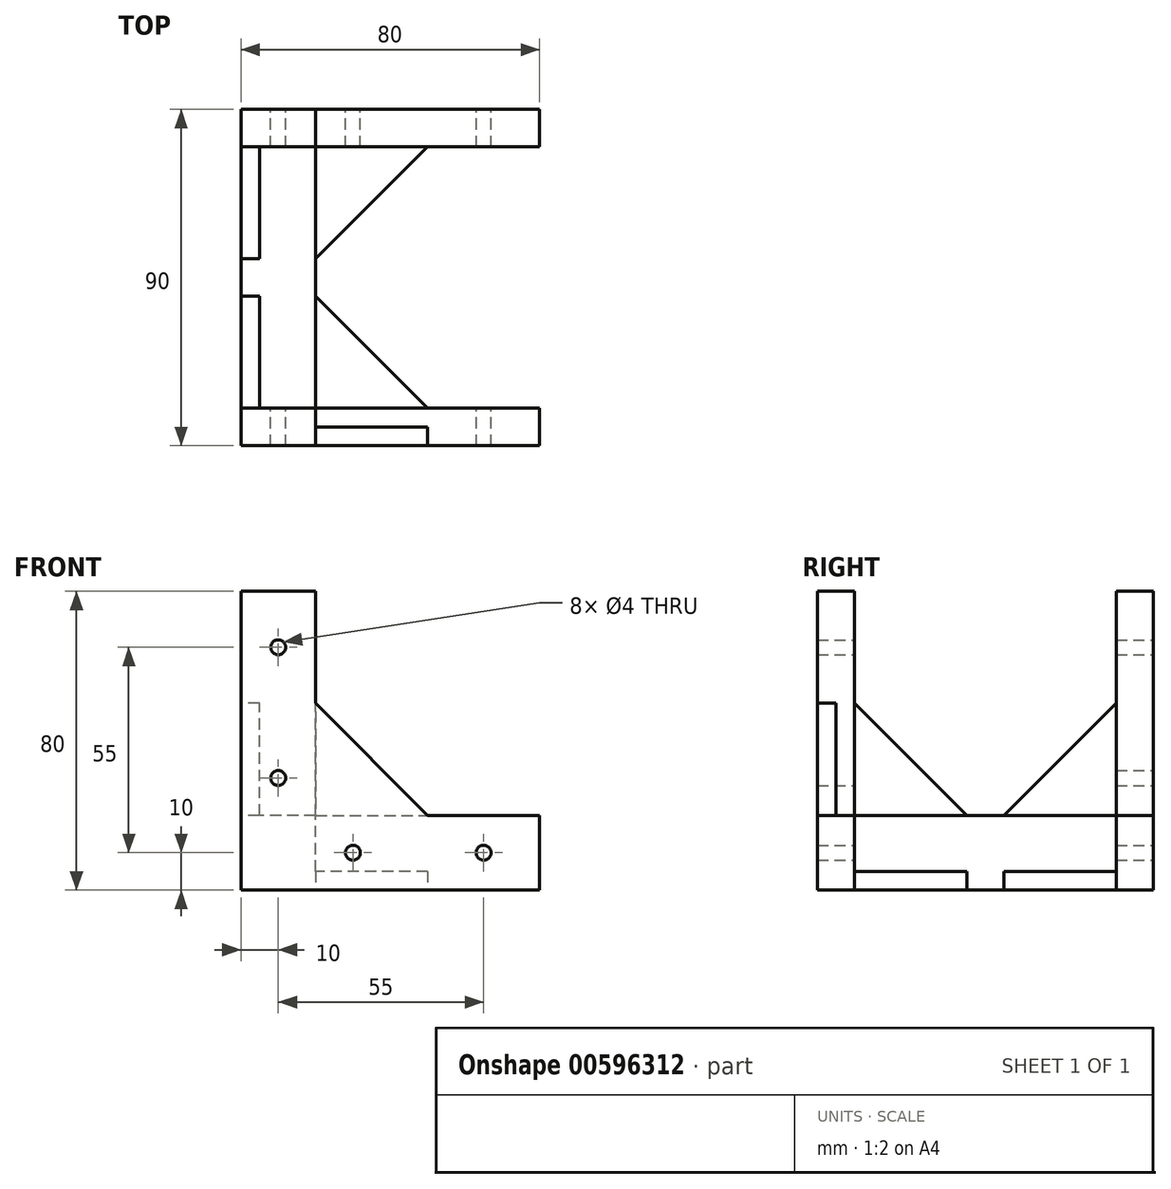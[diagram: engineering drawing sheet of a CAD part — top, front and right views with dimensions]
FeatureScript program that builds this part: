
annotation { "Feature Type Name" : "Feature", "Feature Type Description" : "" }
export const myFeature = defineFeature(function(context is Context, id is Id, definition is map)
    precondition{}
    {
        {
            var Q0;
            Q0=qCreatedBy(makeId("Front.planeOp"),FACE);
            var sketch = newSketch(context, id + "F0", { "sketchPlane" : qUnion([Q0])});
            skLineSegment(sketch, "E0.bottom", {"start": v(0, 0) * mm, "end": v(-20, 0) * mm});
            skLineSegment(sketch, "E0.top", {"start": v(0, 20) * mm, "end": v(-20, 20) * mm});
            skLineSegment(sketch, "E0.left", {"start": v(0, 0) * mm, "end": v(0, 20) * mm});
            skLineSegment(sketch, "E0.right", {"start": v(-20, 0) * mm, "end": v(-20, 20) * mm});
            skSolve(sketch);
        }
        {
            var Q0;
            Q0 = qSketchRegion(id + "F0", true);
            extrude(context, id + "F1", {"entities" : qUnion([Q0]), "depth" : 90 * mm, "offsetDistance" : 25 * mm});
        }
        {
            var Q0;
            Q0=makeQuery(id+"F1.opExtrude","CAP_FACE",FACE,{"disambiguationData":[OSD([sQuery(id+"F0.wireOp",EDGE,"E0.bottom"),sQuery(id+"F0.wireOp",EDGE,"E0.top"),sQuery(id+"F0.wireOp",EDGE,"E0.left"),sQuery(id+"F0.wireOp",EDGE,"E0.right")])],"isStart":false});
            var sketch = newSketch(context, id + "F2", { "sketchPlane" : qUnion([Q0])});
            skLineSegment(sketch, "E1.bottom", {"start": v(-20, 0) * mm, "end": v(0, 0) * mm});
            skLineSegment(sketch, "E1.top", {"start": v(-20, 80) * mm, "end": v(0, 80) * mm});
            skLineSegment(sketch, "E1.left", {"start": v(-20, 0) * mm, "end": v(-20, 80) * mm});
            skLineSegment(sketch, "E1.right", {"start": v(0, 0) * mm, "end": v(0, 80) * mm});
            skLineSegment(sketch, "E2.bottom", {"start": v(-20, 20) * mm, "end": v(60, 20) * mm});
            skLineSegment(sketch, "E2.top", {"start": v(-20, 0) * mm, "end": v(60, 0) * mm});
            skLineSegment(sketch, "E2.left", {"start": v(-20, 20) * mm, "end": v(-20, 0) * mm});
            skLineSegment(sketch, "E2.right", {"start": v(60, 20) * mm, "end": v(60, 0) * mm});
            skSolve(sketch);
        }
        {
            var Q0;
            Q0 = qSketchRegion(id + "F2", true);
            extrude(context, id + "F3", {"entities" : qUnion([Q0]), "operationType" : NewBodyOperationType.ADD, "oppositeDirection" : true, "depth" : 10 * mm, "offsetDistance" : 25 * mm});
        }
        {
            var Q0;
            Q0=makeQuery(id+"F1.opExtrude","CAP_FACE",FACE,{"disambiguationData":[OSD([sQuery(id+"F0.wireOp",EDGE,"E0.bottom"),sQuery(id+"F0.wireOp",EDGE,"E0.top"),sQuery(id+"F0.wireOp",EDGE,"E0.left"),sQuery(id+"F0.wireOp",EDGE,"E0.right")])],"isStart":true});
            var sketch = newSketch(context, id + "F4", { "sketchPlane" : qUnion([Q0])});
            skLineSegment(sketch, "E3.0.0", {"start": v(0, 80) * mm, "end": v(0, 20) * mm});
            skLineSegment(sketch, "E3.0.1", {"start": v(0, 20) * mm, "end": v(20, 20) * mm});
            skLineSegment(sketch, "E3.0.2", {"start": v(20, 20) * mm, "end": v(20, 80) * mm});
            skLineSegment(sketch, "E3.0.3", {"start": v(20, 80) * mm, "end": v(0, 80) * mm});
            skLineSegment(sketch, "E4.0.0", {"start": v(-60, 0) * mm, "end": v(0, 0) * mm});
            skLineSegment(sketch, "E4.0.1", {"start": v(0, 0) * mm, "end": v(0, 20) * mm});
            skLineSegment(sketch, "E4.0.2", {"start": v(0, 20) * mm, "end": v(-60, 20) * mm});
            skLineSegment(sketch, "E4.0.3", {"start": v(-60, 20) * mm, "end": v(-60, 0) * mm});
            skSolve(sketch);
        }
        {
            var Q0;
            Q0 = qSketchRegion(id + "F4", true);
            extrude(context, id + "F5", {"entities" : qUnion([Q0]), "operationType" : NewBodyOperationType.ADD, "oppositeDirection" : true, "depth" : 10 * mm, "offsetDistance" : 25 * mm});
        }
        {
            var Q0;
            Q0=makeQuery(id+"F5.boolean.opBoolean","MERGE",FACE,{"derivedFrom":[makeQuery(id+"F1.opExtrude","CAP_FACE",FACE,{"disambiguationData":[OSD([sQuery(id+"F0.wireOp",EDGE,"E0.bottom"),sQuery(id+"F0.wireOp",EDGE,"E0.top"),sQuery(id+"F0.wireOp",EDGE,"E0.left"),sQuery(id+"F0.wireOp",EDGE,"E0.right")])],"isStart":true}),makeQuery(id+"F5.opExtrude","CAP_FACE",FACE,{"disambiguationData":[OSD([sQuery(id+"F4.wireOp",EDGE,"E3.0.0"),sQuery(id+"F4.wireOp",EDGE,"E3.0.1"),sQuery(id+"F4.wireOp",EDGE,"E3.0.2"),sQuery(id+"F4.wireOp",EDGE,"E3.0.3")])],"isStart":true}),makeQuery(id+"F5.opExtrude","CAP_FACE",FACE,{"disambiguationData":[OSD([sQuery(id+"F4.wireOp",EDGE,"E4.0.0"),sQuery(id+"F4.wireOp",EDGE,"E4.0.1"),sQuery(id+"F4.wireOp",EDGE,"E4.0.2"),sQuery(id+"F4.wireOp",EDGE,"E4.0.3")])],"isStart":true})]});
            var sketch = newSketch(context, id + "F6", { "sketchPlane" : qUnion([Q0])});
            skCircle(sketch, "E5", {"center": v(10, 65) * mm, "radius": 2 * mm});
            skPoint(sketch, "E5.centerSnap0", {"position": v(10, 80) * mm});
            skCircle(sketch, "E6", {"center": v(10, 30) * mm, "radius": 2 * mm});
            skCircle(sketch, "E7", {"center": v(-45, 10) * mm, "radius": 2 * mm});
            skPoint(sketch, "E7.centerSnap0", {"position": v(-60, 10) * mm});
            skCircle(sketch, "E8", {"center": v(-10, 10) * mm, "radius": 2 * mm});
            skSolve(sketch);
        }
        {
            var Q0;
            Q0 = qSketchRegion(id + "F6", true);
            extrude(context, id + "F7", {"entities" : qUnion([Q0]), "operationType" : NewBodyOperationType.REMOVE, "oppositeDirection" : true, "depth" : 116.7 * mm, "offsetDistance" : 25 * mm});
        }
        {
            var Q0;
            Q0=makeQuery(id+"F3.boolean.opBoolean","MERGE",FACE,{"derivedFrom":[makeQuery(id+"F1.opExtrude","CAP_FACE",FACE,{"disambiguationData":[OSD([sQuery(id+"F0.wireOp",EDGE,"E0.bottom"),sQuery(id+"F0.wireOp",EDGE,"E0.top"),sQuery(id+"F0.wireOp",EDGE,"E0.left"),sQuery(id+"F0.wireOp",EDGE,"E0.right")])],"isStart":false}),makeQuery(id+"F3.opExtrude","CAP_FACE",FACE,{"disambiguationData":[OSD([sQuery(id+"F2.wireOp",EDGE,"E1.top"),sQuery(id+"F2.wireOp",EDGE,"E1.left"),sQuery(id+"F2.wireOp",EDGE,"E1.right"),sQuery(id+"F2.wireOp",EDGE,"E2.bottom"),sQuery(id+"F2.wireOp",EDGE,"E2.top"),sQuery(id+"F2.wireOp",EDGE,"E2.left"),sQuery(id+"F2.wireOp",EDGE,"E2.right")])],"isStart":true})]});
            var sketch = newSketch(context, id + "F8", { "sketchPlane" : qUnion([Q0])});
            skLineSegment(sketch, "E9", {"start": v(0, 20) * mm, "end": v(0, 50) * mm});
            skLineSegment(sketch, "E10", {"start": v(0, 50) * mm, "end": v(30, 20) * mm});
            skLineSegment(sketch, "E11", {"start": v(30, 20) * mm, "end": v(0, 20) * mm});
            skSolve(sketch);
        }
        {
            var Q0;
            Q0 = qSketchRegion(id + "F8", true);
            extrude(context, id + "F9", {"entities" : qUnion([Q0]), "operationType" : NewBodyOperationType.ADD, "oppositeDirection" : true, "depth" : 5 * mm, "offsetDistance" : 25 * mm});
        }
        {
            var Q0;
            Q0=makeQuery(id+"F5.boolean.opBoolean","MERGE",FACE,{"derivedFrom":[makeQuery(id+"F3.boolean.opBoolean","MERGE",FACE,{"derivedFrom":[makeQuery(id+"F1.opExtrude","SWEPT_FACE",FACE,{"disambiguationData":[OSD([sQuery(id+"F0.wireOp",EDGE,"E0.bottom")])]}),makeQuery(id+"F3.opExtrude","SWEPT_FACE",FACE,{"disambiguationData":[OSD([sQuery(id+"F2.wireOp",EDGE,"E2.top")])]})]}),makeQuery(id+"F5.opExtrude","SWEPT_FACE",FACE,{"disambiguationData":[OSD([sQuery(id+"F4.wireOp",EDGE,"E4.0.0")])]})]});
            var sketch = newSketch(context, id + "F10", { "sketchPlane" : qUnion([Q0])});
            skLineSegment(sketch, "E12", {"start": v(0, 80) * mm, "end": v(30, 80) * mm});
            skLineSegment(sketch, "E13", {"start": v(30, 10) * mm, "end": v(0, 10) * mm});
            skLineSegment(sketch, "E14", {"start": v(0, 10) * mm, "end": v(0, 40) * mm});
            skLineSegment(sketch, "E15", {"start": v(30, 10) * mm, "end": v(0, 40) * mm});
            skLineSegment(sketch, "E16", {"start": v(0, 80) * mm, "end": v(0, 50) * mm});
            skLineSegment(sketch, "E17", {"start": v(30, 80) * mm, "end": v(0, 50) * mm});
            skSolve(sketch);
        }
        {
            var Q0;
            Q0 = qSketchRegion(id + "F10", true);
            extrude(context, id + "F11", {"entities" : qUnion([Q0]), "operationType" : NewBodyOperationType.ADD, "oppositeDirection" : true, "depth" : 5 * mm, "offsetDistance" : 25 * mm});
        }
        {
            var Q0;
            Q0=makeQuery(id+"F5.boolean.opBoolean","MERGE",FACE,{"derivedFrom":[makeQuery(id+"F3.boolean.opBoolean","MERGE",FACE,{"derivedFrom":[makeQuery(id+"F1.opExtrude","SWEPT_FACE",FACE,{"disambiguationData":[OSD([sQuery(id+"F0.wireOp",EDGE,"E0.right")])]}),makeQuery(id+"F3.opExtrude","SWEPT_FACE",FACE,{"disambiguationData":[OSD([sQuery(id+"F2.wireOp",EDGE,"E1.left"),sQuery(id+"F2.wireOp",EDGE,"E2.left")])]})]}),makeQuery(id+"F5.opExtrude","SWEPT_FACE",FACE,{"disambiguationData":[OSD([sQuery(id+"F4.wireOp",EDGE,"E3.0.2")])]})]});
            var sketch = newSketch(context, id + "F12", { "sketchPlane" : qUnion([Q0])});
            skLineSegment(sketch, "E18", {"start": v(10, 20) * mm, "end": v(10, 50) * mm});
            skLineSegment(sketch, "E19", {"start": v(80, 50) * mm, "end": v(80, 20) * mm});
            skLineSegment(sketch, "E20", {"start": v(10, 20) * mm, "end": v(40, 20) * mm});
            skLineSegment(sketch, "E21", {"start": v(10, 50) * mm, "end": v(40, 20) * mm});
            skLineSegment(sketch, "E22", {"start": v(80, 20) * mm, "end": v(50, 20) * mm});
            skLineSegment(sketch, "E23", {"start": v(80, 50) * mm, "end": v(50, 20) * mm});
            skSolve(sketch);
        }
        {
            var Q0;
            Q0 = qSketchRegion(id + "F12", true);
            extrude(context, id + "F13", {"entities" : qUnion([Q0]), "operationType" : NewBodyOperationType.ADD, "oppositeDirection" : true, "depth" : 5 * mm, "offsetDistance" : 25 * mm});
        }
    });
